# Revit family: Точечный зенитный фонарь M8CITY_Ф_ГЛУХ
name_source: partatom
category: Окна
revit_build: Autodesk Revit 2017 (Build: 20170118_1100(x64)
units: mm (PartAtom-declared; Revit-internal decimal feet)

## family parameters
Всегда вертикально = Нет
Общий = Нет
Основа = Крыша
При загрузке вырезать с полостями = Нет
Точка расчета площади = Нет

## types (1)
- Зенитный фонарь M8CITY Т-Ф
    URL = www.m8city.by
    Высота = 573 мм
    Высота основания = 500 мм
    Длина = 1000 мм
    Длина проёма = 1000 мм
    Длина проёма ввод = 1000 мм
    Изготовитель = ООО Завод М8 Сити Про
    ММ3 = Купол зенитного фонаря Ф : МП молочный 3 мм
    ММ4 = Купол зенитного фонаря Ф : МП молочный 4 мм
    ММ6 = Купол зенитного фонаря Ф : МП молочный 3+3 мм
    ММ7 = Купол зенитного фонаря Ф : МП молочный 3+4 мм
    МП3 = Купол зенитного фонаря Ф : МП прозрачный 3 мм
    МП4 = Купол зенитного фонаря Ф : МП прозрачный 4 мм
    МП6 = Купол зенитного фонаря Ф : МП прозрачный 3+3 мм
    МП7 = Купол зенитного фонаря Ф : МП прозрачный 3+4 мм
    Описание = Точечный зенитный фонарь M8CITY с формованным куполом в глухом исполнении
    Ширина = 1500 мм
    Ширина проёма = 1500 мм
    Ширина проёма ввод = 1500 мм
